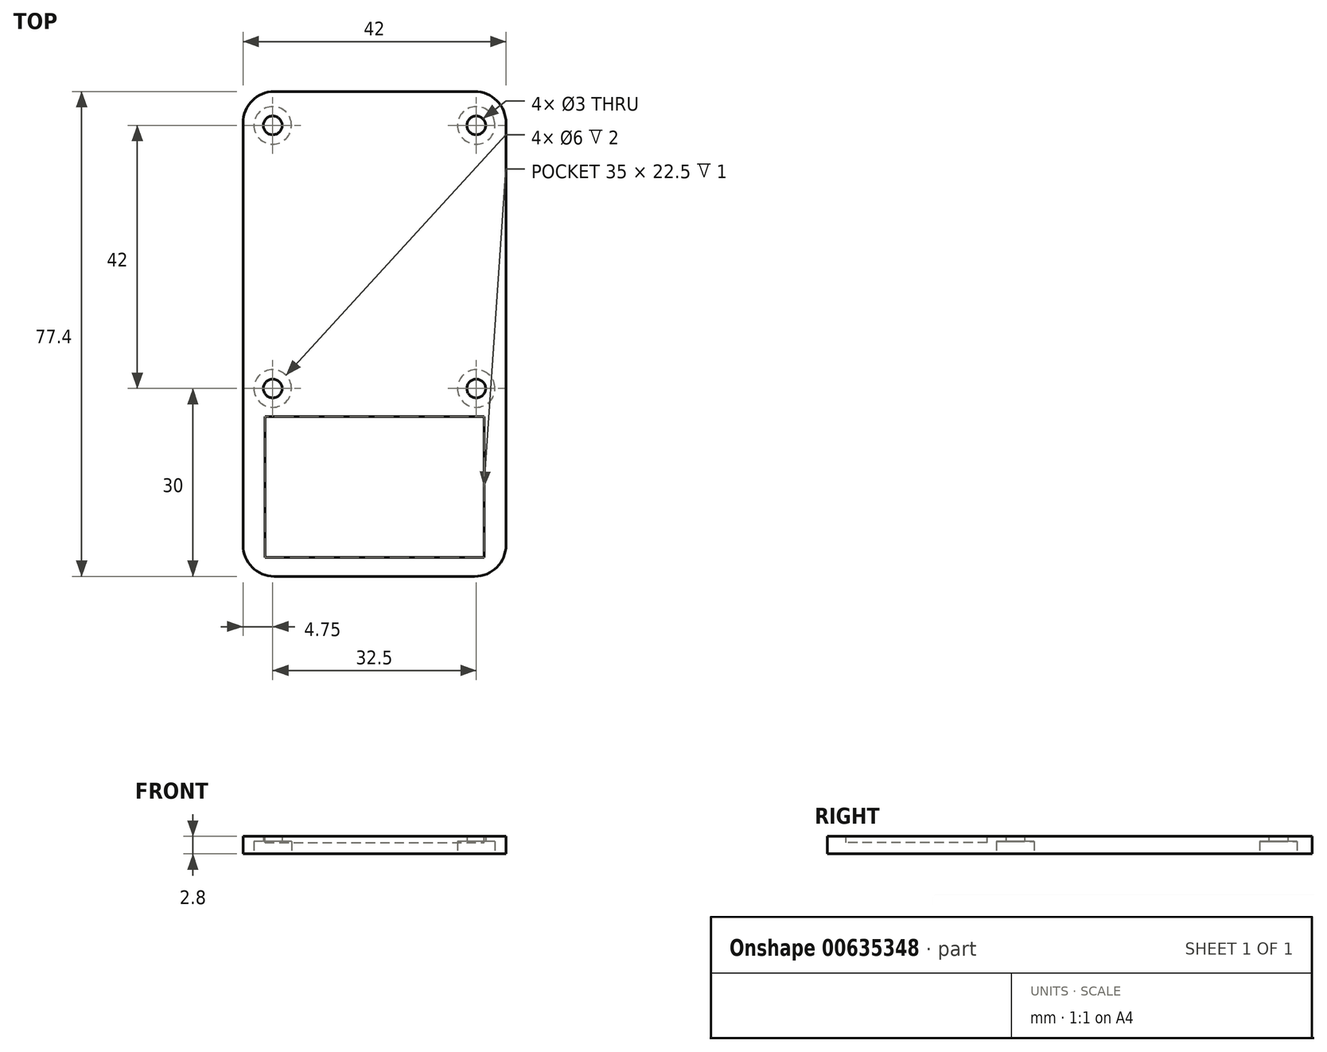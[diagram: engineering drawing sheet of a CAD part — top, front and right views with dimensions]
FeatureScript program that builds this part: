
annotation { "Feature Type Name" : "Feature", "Feature Type Description" : "" }
export const myFeature = defineFeature(function(context is Context, id is Id, definition is map)
    precondition{}
    {
        {
            var Q0;
            Q0=qCreatedBy(makeId("Top.planeOp"),FACE);
            var sketch = newSketch(context, id + "F0", { "sketchPlane" : qUnion([Q0])});
            skLineSegment(sketch, "E0.bottom", {"start": v(-16, 38.7) * mm, "end": v(16, 38.7) * mm});
            skLineSegment(sketch, "E0.top", {"start": v(-16, -38.7) * mm, "end": v(16, -38.7) * mm});
            skLineSegment(sketch, "E0.left", {"start": v(-21, 33.7) * mm, "end": v(-21, -33.7) * mm});
            skLineSegment(sketch, "E0.right", {"start": v(21, 33.7) * mm, "end": v(21, -33.7) * mm});
            skPoint(sketch, "E0.middle", {"position": v(0, 0) * mm});
            skPoint(sketch, "E1.visualSharp", {"position": v(-21, 38.7) * mm});
            skArc(sketch, "E1.filletArc", {"start": v(-16, 38.7) * mm, "mid": v(-19.54, 37.24) * mm, "end": v(-21, 33.7) * mm});
            skPoint(sketch, "E2.visualSharp", {"position": v(21, 38.7) * mm});
            skArc(sketch, "E2.filletArc", {"start": v(21, 33.7) * mm, "mid": v(19.54, 37.24) * mm, "end": v(16, 38.7) * mm});
            skPoint(sketch, "E3.visualSharp", {"position": v(21, -38.7) * mm});
            skArc(sketch, "E3.filletArc", {"start": v(16, -38.7) * mm, "mid": v(19.54, -37.24) * mm, "end": v(21, -33.7) * mm});
            skPoint(sketch, "E4.visualSharp", {"position": v(-21, -38.7) * mm});
            skArc(sketch, "E4.filletArc", {"start": v(-21, -33.7) * mm, "mid": v(-19.54, -37.24) * mm, "end": v(-16, -38.7) * mm});
            skCircle(sketch, "E5", {"center": v(-16.25, 33.3) * mm, "radius": 3 * mm});
            skCircle(sketch, "E6", {"center": v(16.25, 33.3) * mm, "radius": 3 * mm});
            skLineSegment(sketch, "E7", {"start": v(-16.25, 33.3) * mm, "end": v(0, 33.3) * mm});
            skLineSegment(sketch, "E8", {"start": v(0, 33.3) * mm, "end": v(16.25, 33.3) * mm});
            skCircle(sketch, "E9", {"center": v(-16.25, -8.7) * mm, "radius": 3 * mm});
            skCircle(sketch, "E10", {"center": v(16.25, -8.7) * mm, "radius": 3 * mm});
            skLineSegment(sketch, "E11", {"start": v(-16.25, -8.7) * mm, "end": v(0, -8.7) * mm});
            skLineSegment(sketch, "E12", {"start": v(0, -8.7) * mm, "end": v(16.25, -8.7) * mm});
            skCircle(sketch, "E13", {"center": v(-16.25, 33.3) * mm, "radius": 1.5 * mm});
            skCircle(sketch, "E14", {"center": v(16.25, 33.3) * mm, "radius": 1.5 * mm});
            skCircle(sketch, "E15", {"center": v(16.25, -8.7) * mm, "radius": 1.5 * mm});
            skCircle(sketch, "E16", {"center": v(-16.25, -8.7) * mm, "radius": 1.5 * mm});
            skSolve(sketch);
        }
        {
            var Q0;
            Q0=makeQuery(id+"F0.imprint","IMPRINT",FACE,{"disambiguationData":[TD([[makeQuery(id+"F0.imprint","IMPRINT",EDGE,{"derivedFrom":sQuery(id+"F0.wireOp",EDGE,"E0.bottom")}),-1.0]])]});
            var Q1;
            Q1=makeQuery(id+"F0.imprint","IMPRINT",FACE,{"disambiguationData":[TD([[makeQuery(id+"F0.imprint","IMPRINT",EDGE,{"derivedFrom":sQuery(id+"F0.wireOp",EDGE,"E5")}),1.0]])]});
            var Q2;
            Q2=makeQuery(id+"F0.imprint","IMPRINT",FACE,{"disambiguationData":[TD([[makeQuery(id+"F0.imprint","IMPRINT",EDGE,{"derivedFrom":sQuery(id+"F0.wireOp",EDGE,"E6")}),1.0]])]});
            var Q3;
            Q3=makeQuery(id+"F0.imprint","IMPRINT",FACE,{"disambiguationData":[TD([[makeQuery(id+"F0.imprint","IMPRINT",EDGE,{"derivedFrom":sQuery(id+"F0.wireOp",EDGE,"E9")}),1.0]])]});
            var Q4;
            Q4=makeQuery(id+"F0.imprint","IMPRINT",FACE,{"disambiguationData":[TD([[makeQuery(id+"F0.imprint","IMPRINT",EDGE,{"derivedFrom":sQuery(id+"F0.wireOp",EDGE,"E10")}),1.0]])]});
            extrude(context, id + "F1", {"entities" : qUnion([Q0, Q1, Q2, Q3, Q4]), "depth" : 2.8 * mm, "offsetDistance" : 25 * mm});
        }
        {
            var Q0;
            Q0=makeQuery(id+"F0.imprint","IMPRINT",FACE,{"disambiguationData":[TD([[makeQuery(id+"F0.imprint","IMPRINT",EDGE,{"derivedFrom":sQuery(id+"F0.wireOp",EDGE,"E6")}),1.0]])]});
            var Q1;
            Q1=makeQuery(id+"F0.imprint","IMPRINT",FACE,{"disambiguationData":[TD([[makeQuery(id+"F0.imprint","IMPRINT",EDGE,{"derivedFrom":sQuery(id+"F0.wireOp",EDGE,"E5")}),1.0]])]});
            var Q2;
            Q2=makeQuery(id+"F0.imprint","IMPRINT",FACE,{"disambiguationData":[TD([[makeQuery(id+"F0.imprint","IMPRINT",EDGE,{"derivedFrom":sQuery(id+"F0.wireOp",EDGE,"E10")}),1.0]])]});
            var Q3;
            Q3=makeQuery(id+"F0.imprint","IMPRINT",FACE,{"disambiguationData":[TD([[makeQuery(id+"F0.imprint","IMPRINT",EDGE,{"derivedFrom":sQuery(id+"F0.wireOp",EDGE,"E9")}),1.0]])]});
            extrude(context, id + "F2", {"entities" : qUnion([Q0, Q1, Q2, Q3]), "operationType" : NewBodyOperationType.REMOVE, "depth" : 2 * mm, "offsetDistance" : 25 * mm});
        }
        {
            var Q0;
            Q0=makeQuery(id+"F1.opExtrude","CAP_FACE",FACE,{"disambiguationData":[OSD([sQuery(id+"F0.wireOp",EDGE,"E0.bottom"),sQuery(id+"F0.wireOp",EDGE,"E0.top"),sQuery(id+"F0.wireOp",EDGE,"E0.left"),sQuery(id+"F0.wireOp",EDGE,"E0.right"),sQuery(id+"F0.wireOp",EDGE,"E1.filletArc"),sQuery(id+"F0.wireOp",EDGE,"E2.filletArc"),sQuery(id+"F0.wireOp",EDGE,"E3.filletArc"),sQuery(id+"F0.wireOp",EDGE,"E4.filletArc"),sQuery(id+"F0.wireOp",EDGE,"E13"),sQuery(id+"F0.wireOp",EDGE,"E14"),sQuery(id+"F0.wireOp",EDGE,"E15"),sQuery(id+"F0.wireOp",EDGE,"E16")])],"isStart":false});
            var sketch = newSketch(context, id + "F3", { "sketchPlane" : qUnion([Q0])});
            skLineSegment(sketch, "E17.bottom", {"start": v(-17.5, -13.2) * mm, "end": v(17.5, -13.2) * mm});
            skLineSegment(sketch, "E17.top", {"start": v(-17.5, -35.7) * mm, "end": v(17.5, -35.7) * mm});
            skLineSegment(sketch, "E17.left", {"start": v(-17.5, -13.2) * mm, "end": v(-17.5, -35.7) * mm});
            skLineSegment(sketch, "E17.right", {"start": v(17.5, -13.2) * mm, "end": v(17.5, -35.7) * mm});
            skPoint(sketch, "E17.middle", {"position": v(0, -24.45) * mm});
            skSolve(sketch);
        }
        {
            var Q0;
            Q0 = qSketchRegion(id + "F3", true);
            extrude(context, id + "F4", {"entities" : qUnion([Q0]), "operationType" : NewBodyOperationType.REMOVE, "oppositeDirection" : true, "depth" : 1 * mm, "offsetDistance" : 25 * mm});
        }
    });
